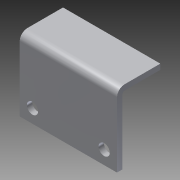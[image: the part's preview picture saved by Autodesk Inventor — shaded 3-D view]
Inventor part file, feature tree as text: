
AUTODESK INVENTOR PART (.ipt)
format: ipt  version: 2013 (Build 170138000, 138)  size: 181,248 bytes
history: native  units: in
note: dims shown in document units (in); Inventor stores cm internally (conversion verified against a paired STEP export)
features: sketch x6, other x6, sheet_metal_op x4, reference x2, extrude x1
ambient origin geometry x8: Origin, YZ Plane, XZ Plane, XY Plane, X Axis, Y Axis, Z Axis, Center Point
bodies: Solid1 (feature_tree)
feature tree (19):
  sheet_metal_op  "Face1"
  sheet_metal_op  "Flange1"
  extrude  "Extrusion1"  Depth=1.5in
  sketch  "Sketch1"  dims[d1=4.297in d2=1.5in]
  other  "Plate1"
  sketch  "Sketch2"  dims[d3=0.295in]
  other  "Plate2"
  sheet_metal_op  "Bend1"
  sheet_metal_op  "Corner1"
  sketch  "Sketch8"  dims[d4=1.181in]
  reference  "Reference1"
  reference  "Reference2"
  sketch  "Sketch10"  dims[d5=0.295in]
  sketch  "Sketch14"  dims[d8=0.125in]
  sketch  "Sketch15"  dims[d9=0.125in d10=0.0625in d11=0.25in d12=0.125in d13=1.0in d14=90.0deg d15=0.05in d16=0.5in d17=0.125in d18=0.125in d19=0.125in d20=0.0in d21=2.0in d22=2.053in d23=1.0in d24=0.0in d29=0.125in d30=0.0in d31=0.125in d32=0.0in d0=1.582in d6=0.0625in d7=0.125in]
  other  "Cut1"
  other  "Cut3"
  other  "Cut4"
  other  "Definition1"
